# Revit family: Haworth_Masters_Table_Round
name_source: partatom
category: Furniture Systems
revit_build: Autodesk Revit 2018 (Build: 20170223_1515(x64)
units: mm (PartAtom-declared; Revit-internal decimal feet)

## family parameters
Always vertical = Yes
Cut with Voids When Loaded = No
OmniClass Number = 23.40.70.14.64.21
OmniClass Title = Systems Furniture
Part Type = Normal
Room Calculation Point = No
Round Connector Dimension = Use Diameter
Shared = No
Work Plane-Based = No

## types (1)
- 36" Diameter
    Actual Height = 29"
    Actual Width = 36"
    Assembly Code = E2020200
    Base Finish = Haworth _ Paint _ Metallic Champagne
    Custom Size = No
    Description = Haworth - Masters - Table - Round
    Disc Base Radius = 10 1/2"
    Height = 29"
    Leg Height = 27 1/2"
    Manufacturer = Haworth
    Max. Height = 29"
    Max. Width = 48"
    Min. Height = 29"
    Min. Width = 30"
    Model = Haworth - Masters - Table - Round
    Revision Number = 2
    Size = Verify Final Dim. w/ Haworth
    Sustainability Info = http://www.haworth.com
    Table Edge Finish = Haworth _ Wood _ White Oak
    Table Finish = Haworth _ Wood _ White Oak
    Table Thickness = 1 1/2"
    URL = http://www.haworth.com
    URL - Product = http://www.haworth.com
    Warranty = http://www.haworth.com
    Width = 36"

## geometry (parser evidence)
native form markers: Sweep x4
no freeform markers — native parametric forms only
